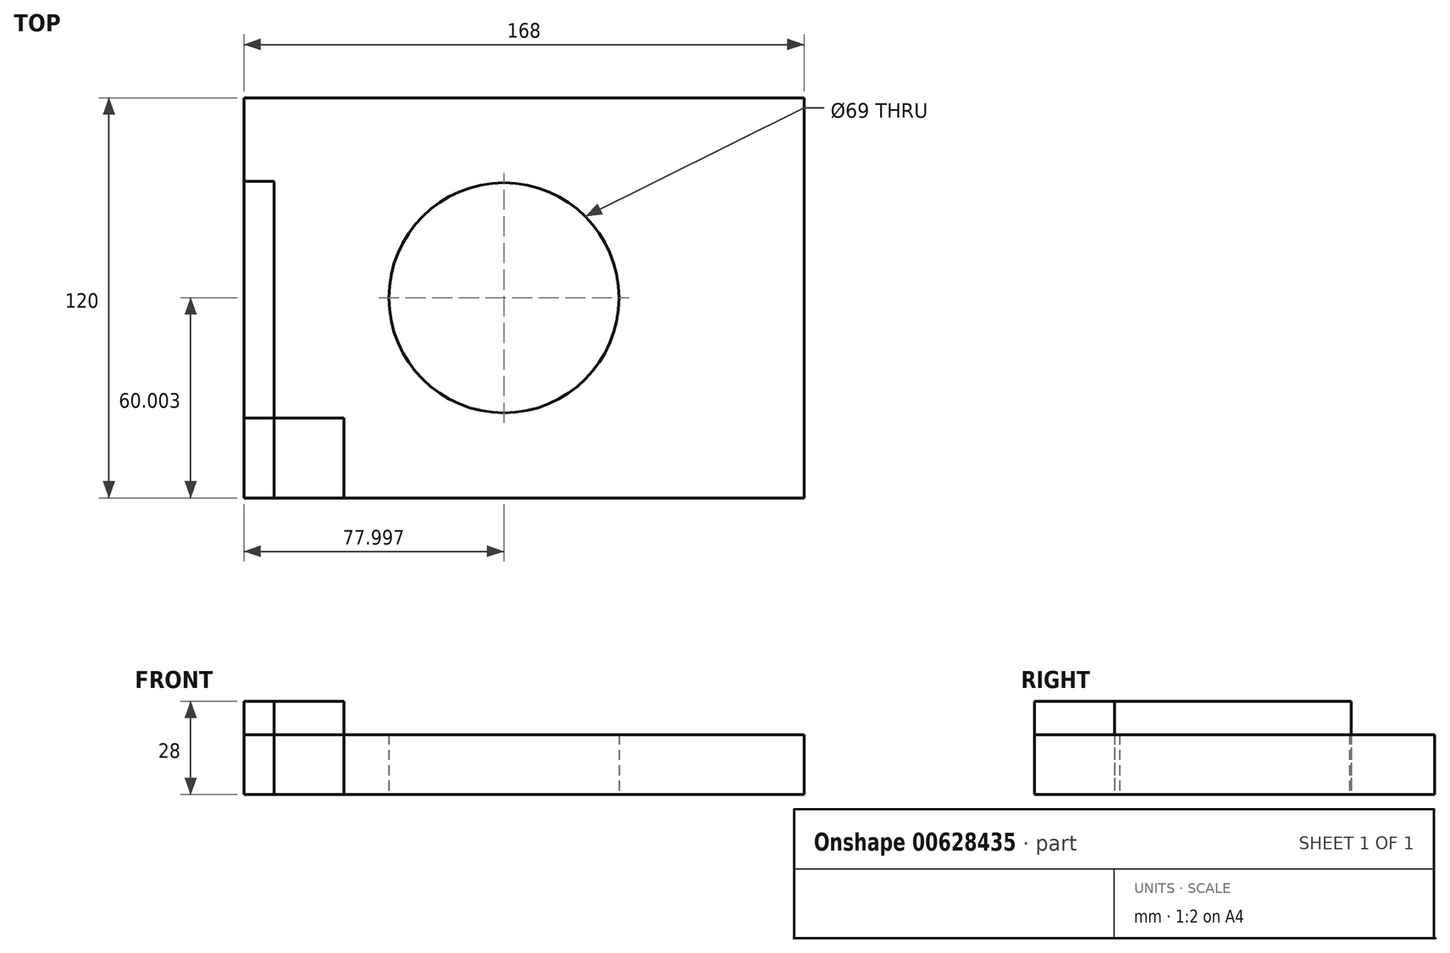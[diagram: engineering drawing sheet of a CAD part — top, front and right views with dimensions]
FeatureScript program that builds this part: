
annotation { "Feature Type Name" : "Feature", "Feature Type Description" : "" }
export const myFeature = defineFeature(function(context is Context, id is Id, definition is map)
    precondition{}
    {
        {
            var Q0;
            Q0=qCreatedBy(makeId("Top.planeOp"),FACE);
            var sketch = newSketch(context, id + "F0", { "sketchPlane" : qUnion([Q0])});
            skLineSegment(sketch, "E0.bottom", {"start": v(-81.58, 70.21) * mm, "end": v(86.42, 70.21) * mm});
            skLineSegment(sketch, "E0.top", {"start": v(-81.58, -49.79) * mm, "end": v(86.42, -49.79) * mm});
            skLineSegment(sketch, "E0.left", {"start": v(-81.58, 70.21) * mm, "end": v(-81.58, -49.79) * mm});
            skLineSegment(sketch, "E0.right", {"start": v(86.42, 70.21) * mm, "end": v(86.42, -49.79) * mm});
            skCircle(sketch, "E1", {"center": v(-3.58, 10.21) * mm, "radius": 48 * mm});
            skLineSegment(sketch, "E2.bottom", {"start": v(-81.58, -49.79) * mm, "end": v(-72.58, -49.79) * mm});
            skLineSegment(sketch, "E2.top", {"start": v(-81.58, 45.21) * mm, "end": v(-72.58, 45.21) * mm});
            skLineSegment(sketch, "E2.left", {"start": v(-81.58, -49.79) * mm, "end": v(-81.58, 45.21) * mm});
            skLineSegment(sketch, "E2.right", {"start": v(-72.58, -49.79) * mm, "end": v(-72.58, 45.21) * mm});
            skLineSegment(sketch, "E3.bottom", {"start": v(-81.58, -49.79) * mm, "end": v(-51.58, -49.79) * mm});
            skLineSegment(sketch, "E3.top", {"start": v(-81.58, -25.79) * mm, "end": v(-51.58, -25.79) * mm});
            skLineSegment(sketch, "E3.left", {"start": v(-81.58, -49.79) * mm, "end": v(-81.58, -25.79) * mm});
            skLineSegment(sketch, "E3.right", {"start": v(-51.58, -49.79) * mm, "end": v(-51.58, -25.79) * mm});
            skLineSegment(sketch, "E4.bottom", {"start": v(86.42, -49.79) * mm, "end": v(44.42, -49.79) * mm});
            skLineSegment(sketch, "E4.top", {"start": v(86.42, -25.79) * mm, "end": v(44.42, -25.79) * mm});
            skLineSegment(sketch, "E4.left", {"start": v(86.42, -49.79) * mm, "end": v(86.42, -25.79) * mm});
            skLineSegment(sketch, "E4.right", {"start": v(44.42, -49.79) * mm, "end": v(44.42, -25.79) * mm});
            skCircle(sketch, "E5", {"center": v(-3.58, 10.21) * mm, "radius": 34.5 * mm});
            skSolve(sketch);
        }
        {
            var Q0;
            {var subQ0=sQuery(id+"F0.wireOp",EDGE,"E2.top");Q0=makeQuery(id+"F0.imprint","IMPRINT",FACE,{"disambiguationData":[TD([[makeQuery(id+"F0.imprint","IMPRINT",EDGE,{"derivedFrom":subQ0}),-1.0]])]});}
            var Q1;
            {var subQ5=sQuery(id+"F0.wireOp",EDGE,"E3.left");Q1=makeQuery(id+"F0.imprint","IMPRINT",FACE,{"disambiguationData":[TD([[makeQuery(id+"F0.imprint","IMPRINT",EDGE,{"derivedFrom":subQ5}),-1.0]])]});}
            var Q2;
            {var subQ5=sQuery(id+"F0.wireOp",EDGE,"E3.right");Q2=makeQuery(id+"F0.imprint","IMPRINT",FACE,{"disambiguationData":[TD([[makeQuery(id+"F0.imprint","IMPRINT",EDGE,{"derivedFrom":subQ5}),1.0]])]});}
            var Q3;
            Q3=makeQuery(id+"F0.imprint","IMPRINT",FACE,{"disambiguationData":[TD([[makeQuery(id+"F0.imprint","IMPRINT",EDGE,{"derivedFrom":sQuery(id+"F0.wireOp",EDGE,"E4.bottom")}),-1.0]])]});
            extrude(context, id + "F1", {"entities" : qUnion([Q0, Q1, Q2, Q3]), "depth" : 28 * mm, "offsetDistance" : 25 * mm});
        }
        {
            var Q0;
            Q0 = qSketchRegion(id + "F0", true);
            var Q1;
            Q1=makeQuery(id+"F0.imprint","IMPRINT",FACE,{"disambiguationData":[TD([[makeQuery(id+"F0.imprint","IMPRINT",EDGE,{"derivedFrom":sQuery(id+"F0.wireOp",EDGE,"E0.bottom")}),-1.0]])]});
            extrude(context, id + "F2", {"entities" : qUnion([Q0, Q1]), "depth" : 18 * mm, "offsetDistance" : 25 * mm});
        }
        {
            var Q0;
            Q0=makeQuery(id+"F0.imprint","IMPRINT",FACE,{"disambiguationData":[TD([[makeQuery(id+"F0.imprint","IMPRINT",EDGE,{"derivedFrom":sQuery(id+"F0.wireOp",EDGE,"E1")}),1.0]])]});
            extrude(context, id + "F3", {"entities" : qUnion([Q0]), "operationType" : NewBodyOperationType.ADD, "depth" : 18 * mm, "offsetDistance" : 25 * mm});
        }
    });
